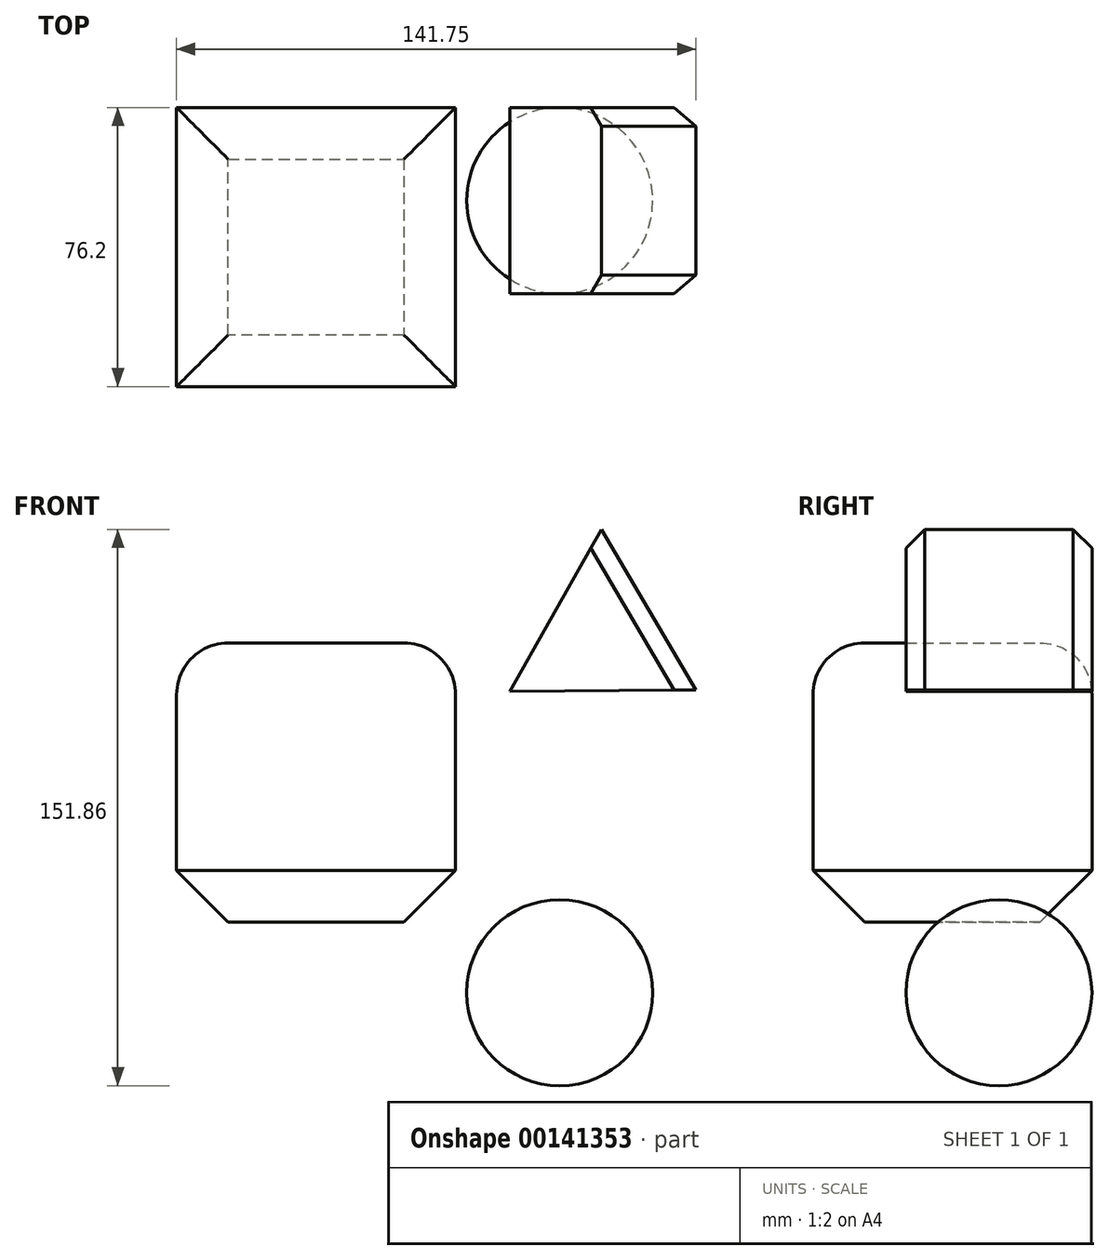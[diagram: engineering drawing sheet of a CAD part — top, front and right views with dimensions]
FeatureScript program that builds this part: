
annotation { "Feature Type Name" : "Feature", "Feature Type Description" : "" }
export const myFeature = defineFeature(function(context is Context, id is Id, definition is map)
    precondition{}
    {
        {
            var Q0;
            Q0=qCreatedBy(makeId("Front.planeOp"),FACE);
            var sketch = newSketch(context, id + "F0", { "sketchPlane" : qUnion([Q0])});
            skLineSegment(sketch, "E0.bottom", {"start": v(10.53, -18.73) * mm, "end": v(-65.67, -18.73) * mm});
            skLineSegment(sketch, "E0.top", {"start": v(10.53, 57.47) * mm, "end": v(-65.67, 57.47) * mm});
            skLineSegment(sketch, "E0.left", {"start": v(10.53, -18.73) * mm, "end": v(10.53, 57.47) * mm});
            skLineSegment(sketch, "E0.right", {"start": v(-65.67, -18.73) * mm, "end": v(-65.67, 57.47) * mm});
            skPoint(sketch, "E0.middle", {"position": v(-27.57, 19.37) * mm});
            skSolve(sketch);
        }
        {
            var Q0;
            Q0 = qSketchRegion(id + "F0", true);
            extrude(context, id + "F1", {"entities" : qUnion([Q0]), "depth" : 76.2 * mm});
        }
        {
            var Q0;
            Q0=makeQuery(id+"F1.opExtrude","SWEPT_EDGE",EDGE,{"disambiguationData":[OSD([sQuery(id+"F0.wireOp",EDGE,"E0.top"),sQuery(id+"F0.wireOp",EDGE,"E0.right")])]});
            var Q1;
            Q1=makeQuery(id+"F1.opExtrude","CAP_EDGE",EDGE,{"disambiguationData":[OSD([sQuery(id+"F0.wireOp",EDGE,"E0.top")])],"isStart":true});
            var Q2;
            Q2=makeQuery(id+"F1.opExtrude","SWEPT_EDGE",EDGE,{"disambiguationData":[OSD([sQuery(id+"F0.wireOp",EDGE,"E0.top"),sQuery(id+"F0.wireOp",EDGE,"E0.left")])]});
            var Q3;
            Q3=makeQuery(id+"F1.opExtrude","CAP_EDGE",EDGE,{"disambiguationData":[OSD([sQuery(id+"F0.wireOp",EDGE,"E0.top")])],"isStart":false});
            fillet(context, id + "F2", {"entities" : qUnion([Q0, Q1, Q2, Q3]), "radius" : 14.1 * mm, "tangentPropagation" : true, "allowEdgeOverflow" : false});
        }
        {
            var Q0;
            Q0=makeQuery(id+"F1.opExtrude","SWEPT_EDGE",EDGE,{"disambiguationData":[OSD([sQuery(id+"F0.wireOp",EDGE,"E0.bottom"),sQuery(id+"F0.wireOp",EDGE,"E0.right")])]});
            var Q1;
            Q1=makeQuery(id+"F1.opExtrude","CAP_EDGE",EDGE,{"disambiguationData":[OSD([sQuery(id+"F0.wireOp",EDGE,"E0.bottom")])],"isStart":false});
            var Q2;
            Q2=makeQuery(id+"F1.opExtrude","SWEPT_EDGE",EDGE,{"disambiguationData":[OSD([sQuery(id+"F0.wireOp",EDGE,"E0.bottom"),sQuery(id+"F0.wireOp",EDGE,"E0.left")])]});
            var Q3;
            Q3=makeQuery(id+"F1.opExtrude","CAP_EDGE",EDGE,{"disambiguationData":[OSD([sQuery(id+"F0.wireOp",EDGE,"E0.bottom")])],"isStart":true});
            chamfer(context, id + "F3", {"entities" : qUnion([Q0, Q1, Q2, Q3]), "width" : 14.1 * mm, "tangentPropagation" : true});
        }
        {
            var Q0;
            Q0=qCreatedBy(makeId("Front.planeOp"),FACE);
            var sketch = newSketch(context, id + "F4", { "sketchPlane" : qUnion([Q0])});
            skCircle(sketch, "E1", {"center": v(38.97, -38.03) * mm, "radius": 25.4 * mm});
            skSolve(sketch);
        }
        {
            var Q0;
            Q0 = qSketchRegion(id + "F4", true);
            extrude(context, id + "F5", {"entities" : qUnion([Q0]), "depth" : 50.8 * mm});
        }
        {
            var Q0;
            Q0=makeQuery(id+"F5.opExtrude","CAP_EDGE",EDGE,{"disambiguationData":[OSD([sQuery(id+"F4.wireOp",EDGE,"E1")])],"isStart":false});
            var Q1;
            Q1=makeQuery(id+"F5.opExtrude","CAP_EDGE",EDGE,{"disambiguationData":[OSD([sQuery(id+"F4.wireOp",EDGE,"E1")])],"isStart":true});
            fillet(context, id + "F6", {"entities" : qUnion([Q0, Q1]), "radius" : 25.4 * mm, "tangentPropagation" : true, "allowEdgeOverflow" : false});
        }
        {
            var Q0;
            Q0=qCreatedBy(makeId("Front.planeOp"),FACE);
            var sketch = newSketch(context, id + "F7", { "sketchPlane" : qUnion([Q0])});
            skCircle(sketch, "E2.cCircle", {"center": v(50.56, 59.1) * mm, "radius": 14.66 * mm, "construction": true});
            skLineSegment(sketch, "E2.0", {"start": v(50.3, 88.43) * mm, "end": v(76.08, 44.65) * mm});
            skLineSegment(sketch, "E2.1", {"start": v(76.08, 44.65) * mm, "end": v(25.29, 44.22) * mm});
            skLineSegment(sketch, "E2.2", {"start": v(25.29, 44.22) * mm, "end": v(50.3, 88.43) * mm});
            skPoint(sketch, "E2.0.midPoint", {"position": v(63.2, 66.54) * mm});
            skSolve(sketch);
        }
        {
            var Q0;
            Q0 = qSketchRegion(id + "F7", true);
            extrude(context, id + "F8", {"entities" : qUnion([Q0]), "depth" : 50.8 * mm});
        }
        {
            var Q0;
            Q0=makeQuery(id+"F8.opExtrude","CAP_EDGE",EDGE,{"disambiguationData":[OSD([sQuery(id+"F7.wireOp",EDGE,"E2.0")])],"isStart":true});
            var Q1;
            Q1=makeQuery(id+"F8.opExtrude","CAP_EDGE",EDGE,{"disambiguationData":[OSD([sQuery(id+"F7.wireOp",EDGE,"E2.0")])],"isStart":false});
            chamfer(context, id + "F9", {"entities" : qUnion([Q0, Q1]), "chamferType" : ChamferType.TWO_OFFSETS, "width1" : 5.08 * mm, "oppositeDirection" : false, "width2" : 5.08 * mm, "tangentPropagation" : true});
        }
    });
